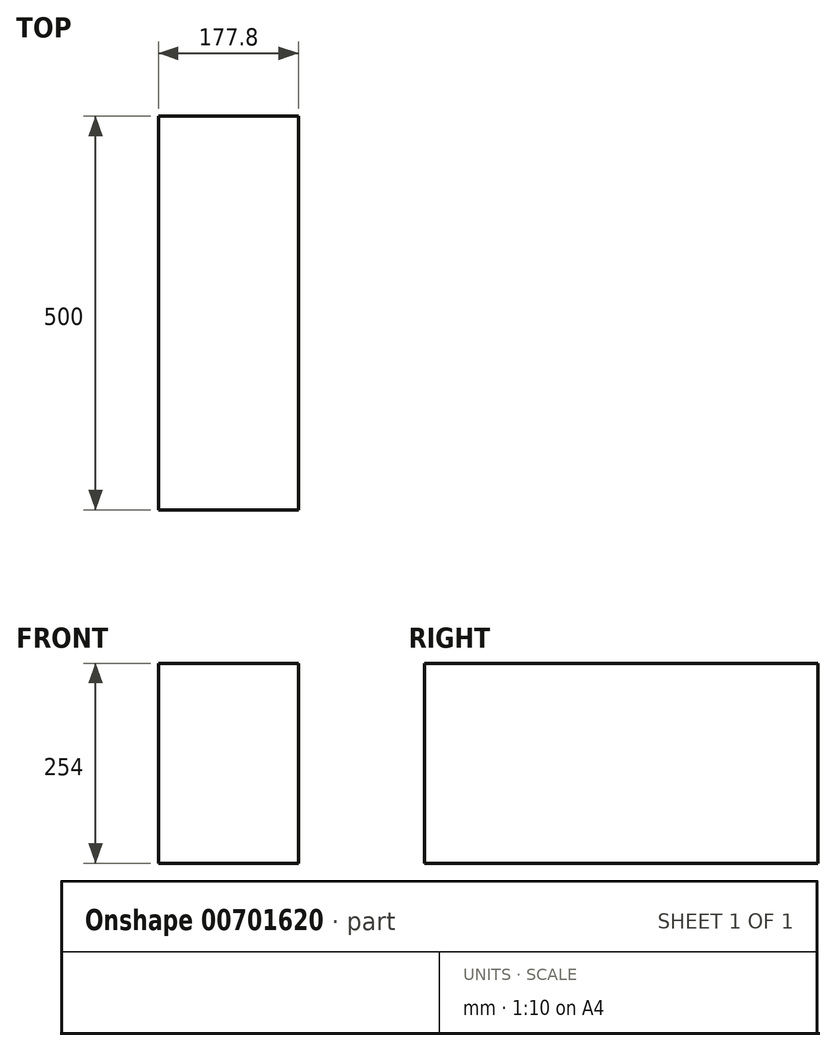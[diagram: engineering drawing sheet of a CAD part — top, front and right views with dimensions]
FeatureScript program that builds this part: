
annotation { "Feature Type Name" : "Feature", "Feature Type Description" : "" }
export const myFeature = defineFeature(function(context is Context, id is Id, definition is map)
    precondition{}
    {
        {
            var Q0;
            Q0=qCreatedBy(makeId("Front.planeOp"),FACE);
            var sketch = newSketch(context, id + "F0", { "sketchPlane" : qUnion([Q0])});
            skLineSegment(sketch, "E0.bottom", {"start": v(88.9, -127) * mm, "end": v(-88.9, -127) * mm});
            skLineSegment(sketch, "E0.top", {"start": v(88.9, 127) * mm, "end": v(-88.9, 127) * mm});
            skLineSegment(sketch, "E0.left", {"start": v(88.9, -127) * mm, "end": v(88.9, 127) * mm});
            skLineSegment(sketch, "E0.right", {"start": v(-88.9, -127) * mm, "end": v(-88.9, 127) * mm});
            skPoint(sketch, "E0.middle", {"position": v(0, 0) * mm});
            skSolve(sketch);
        }
        {
            var Q0;
            Q0=makeQuery(id+"F0.imprint","IMPRINT",FACE,{"disambiguationData":[TD([[makeQuery(id+"F0.imprint","IMPRINT",EDGE,{"derivedFrom":sQuery(id+"F0.wireOp",EDGE,"E0.bottom")}),-1.0]])]});
            extrude(context, id + "F1", {"entities" : qUnion([Q0]), "depth" : 500 * mm, "offsetDistance" : 25.4 * mm, "symmetric" : true});
        }
    });
